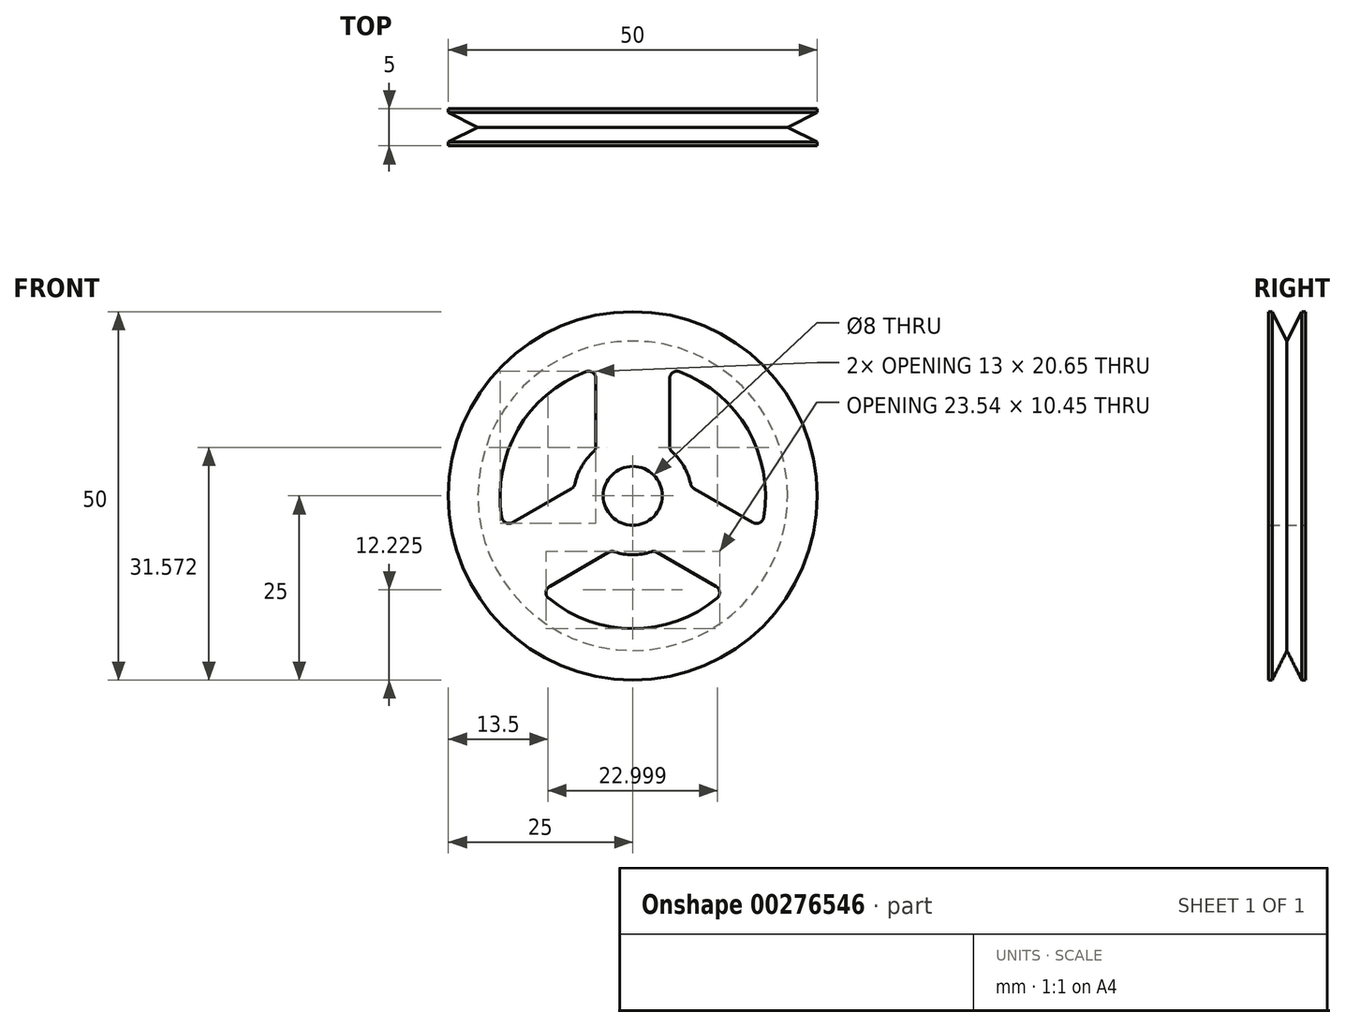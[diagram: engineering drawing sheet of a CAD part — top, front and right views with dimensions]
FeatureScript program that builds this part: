
annotation { "Feature Type Name" : "Feature", "Feature Type Description" : "" }
export const myFeature = defineFeature(function(context is Context, id is Id, definition is map)
    precondition{}
    {
        {
            var Q0;
            Q0=qCreatedBy(makeId("Front.planeOp"),FACE);
            var sketch = newSketch(context, id + "F0", { "sketchPlane" : qUnion([Q0])});
            skCircle(sketch, "E0", {"center": v(0, 0) * mm, "radius": 25 * mm});
            skArc(sketch, "E1.0", {"start": v(-6.35, 16.84) * mm, "mid": v(-15.59, 9) * mm, "end": v(-17.76, -2.92) * mm});
            skArc(sketch, "E2", {"start": v(-5.33, 5.96) * mm, "mid": v(-6.93, 4) * mm, "end": v(-7.83, 1.64) * mm});
            skCircle(sketch, "E3", {"center": v(0, 0) * mm, "radius": 4 * mm});
            skLineSegment(sketch, "E4.0", {"start": v(5, 6.7) * mm, "end": v(5, 15.9) * mm});
            skLineSegment(sketch, "E5.0", {"start": v(-5, 6.7) * mm, "end": v(-5, 15.9) * mm});
            skLineSegment(sketch, "E6.1.0", {"start": v(-3.3, -7.68) * mm, "end": v(-11.27, -12.28) * mm});
            skLineSegment(sketch, "E6.1.1", {"start": v(-8.3, 0.98) * mm, "end": v(-16.27, -3.62) * mm});
            skLineSegment(sketch, "E6.2.0", {"start": v(8.3, 0.98) * mm, "end": v(16.27, -3.62) * mm});
            skLineSegment(sketch, "E6.2.1", {"start": v(3.3, -7.68) * mm, "end": v(11.27, -12.28) * mm});
            skArc(sketch, "E7.trimOffspring", {"start": v(-2.5, -7.6) * mm, "mid": v(0, -8) * mm, "end": v(2.5, -7.6) * mm});
            skArc(sketch, "E8.trimOffspring", {"start": v(-11.4, -13.92) * mm, "mid": v(0, -18) * mm, "end": v(11.4, -13.92) * mm});
            skArc(sketch, "E9.trimOffspring", {"start": v(7.83, 1.64) * mm, "mid": v(6.93, 4) * mm, "end": v(5.33, 5.96) * mm});
            skArc(sketch, "E10.trimOffspring", {"start": v(17.76, -2.92) * mm, "mid": v(15.59, 9) * mm, "end": v(6.35, 16.84) * mm});
            skPoint(sketch, "E11.visualSharp", {"position": v(-5, 17.3) * mm});
            skArc(sketch, "E11.filletArc", {"start": v(-5, 15.9) * mm, "mid": v(-5.43, 16.73) * mm, "end": v(-6.35, 16.84) * mm});
            skPoint(sketch, "E12.visualSharp", {"position": v(-5, 6.24) * mm});
            skArc(sketch, "E12.filletArc", {"start": v(-5.33, 5.96) * mm, "mid": v(-5.09, 6.3) * mm, "end": v(-5, 6.7) * mm});
            skPoint(sketch, "E13.visualSharp", {"position": v(-7.9, 1.2) * mm});
            skArc(sketch, "E13.filletArc", {"start": v(-8.3, 0.98) * mm, "mid": v(-8, 1.26) * mm, "end": v(-7.83, 1.64) * mm});
            skPoint(sketch, "E14.visualSharp", {"position": v(-17.47, -4.32) * mm});
            skArc(sketch, "E14.filletArc", {"start": v(-17.76, -2.92) * mm, "mid": v(-17.2, -3.66) * mm, "end": v(-16.27, -3.62) * mm});
            skPoint(sketch, "E15.visualSharp", {"position": v(-2.9, -7.45) * mm});
            skArc(sketch, "E15.filletArc", {"start": v(-2.5, -7.6) * mm, "mid": v(-2.91, -7.56) * mm, "end": v(-3.3, -7.68) * mm});
            skPoint(sketch, "E16.visualSharp", {"position": v(2.9, -7.45) * mm});
            skArc(sketch, "E16.filletArc", {"start": v(3.3, -7.68) * mm, "mid": v(2.91, -7.56) * mm, "end": v(2.5, -7.6) * mm});
            skPoint(sketch, "E17.visualSharp", {"position": v(-12.47, -12.98) * mm});
            skArc(sketch, "E17.filletArc", {"start": v(-11.27, -12.28) * mm, "mid": v(-11.77, -13.07) * mm, "end": v(-11.4, -13.92) * mm});
            skPoint(sketch, "E18.visualSharp", {"position": v(12.47, -12.98) * mm});
            skArc(sketch, "E18.filletArc", {"start": v(11.4, -13.92) * mm, "mid": v(11.77, -13.07) * mm, "end": v(11.27, -12.28) * mm});
            skPoint(sketch, "E19.visualSharp", {"position": v(7.9, 1.2) * mm});
            skArc(sketch, "E19.filletArc", {"start": v(7.83, 1.64) * mm, "mid": v(8, 1.26) * mm, "end": v(8.3, 0.98) * mm});
            skPoint(sketch, "E20.visualSharp", {"position": v(17.47, -4.32) * mm});
            skArc(sketch, "E20.filletArc", {"start": v(16.27, -3.62) * mm, "mid": v(17.2, -3.66) * mm, "end": v(17.76, -2.92) * mm});
            skPoint(sketch, "E21.visualSharp", {"position": v(5, 17.3) * mm});
            skArc(sketch, "E21.filletArc", {"start": v(6.35, 16.84) * mm, "mid": v(5.43, 16.73) * mm, "end": v(5, 15.9) * mm});
            skPoint(sketch, "E22.visualSharp", {"position": v(5, 6.24) * mm});
            skArc(sketch, "E22.filletArc", {"start": v(5, 6.7) * mm, "mid": v(5.09, 6.3) * mm, "end": v(5.33, 5.96) * mm});
            skSolve(sketch);
        }
        {
            var Q0;
            Q0 = qSketchRegion(id + "F0", true);
            extrude(context, id + "F1", {"entities" : qUnion([Q0]), "endBound" : BoundingType.SYMMETRIC, "depth" : 5 * mm});
        }
        {
            var Q0;
            Q0=qCreatedBy(makeId("Right.planeOp"),FACE);
            var sketch = newSketch(context, id + "F2", { "sketchPlane" : qUnion([Q0])});
            skLineSegment(sketch, "E23", {"start": v(0, 21) * mm, "end": v(0, 25) * mm});
            skLineSegment(sketch, "E24", {"start": v(0, 25) * mm, "end": v(-2, 25) * mm});
            skLineSegment(sketch, "E25", {"start": v(-2, 25) * mm, "end": v(0, 21) * mm});
            skLineSegment(sketch, "E26.MirrorCS", {"start": v(0, 25) * mm, "end": v(2, 25) * mm});
            skLineSegment(sketch, "E27.MirrorCS", {"start": v(2, 25) * mm, "end": v(0, 21) * mm});
            skLineSegment(sketch, "E28", {"start": v(-15.9, 0) * mm, "end": v(15.91, 0) * mm, "construction": true});
            skSolve(sketch);
        }
        {
            var Q0;
            Q0 = qSketchRegion(id + "F2", true);
            var Q1;
            Q1=sQuery(id+"F2.wireOp",EDGE,"E28");
            revolve(context, id + "F3", {"operationType" : NewBodyOperationType.REMOVE, "entities" : qUnion([Q0]), "axis" : qUnion([Q1]), "revolveType" : RevolveType.FULL});
        }
    });
